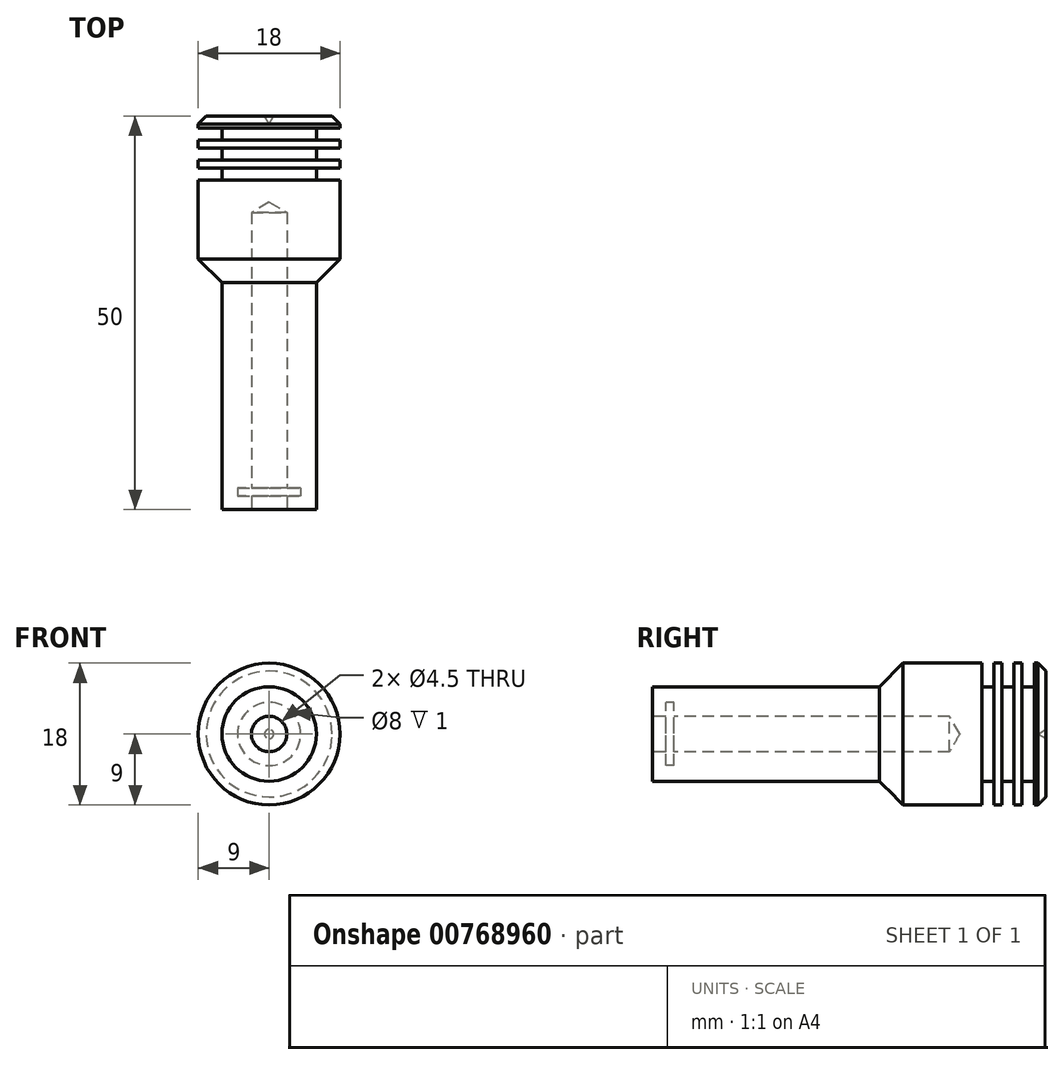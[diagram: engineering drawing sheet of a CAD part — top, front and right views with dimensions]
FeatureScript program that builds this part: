
annotation { "Feature Type Name" : "Feature", "Feature Type Description" : "" }
export const myFeature = defineFeature(function(context is Context, id is Id, definition is map)
    precondition{}
    {
        {
            var Q0;
            Q0=qCreatedBy(makeId("Right.planeOp"),FACE);
            var sketch = newSketch(context, id + "F0", { "sketchPlane" : qUnion([Q0])});
            skLineSegment(sketch, "E0", {"start": v(0, 6) * mm, "end": v(28.85, 6) * mm});
            skLineSegment(sketch, "E1", {"start": v(28.85, 6) * mm, "end": v(31.85, 9) * mm});
            skLineSegment(sketch, "E2", {"start": v(31.85, 9) * mm, "end": v(41.85, 9) * mm});
            skLineSegment(sketch, "E3", {"start": v(41.85, 9) * mm, "end": v(41.85, 6) * mm});
            skLineSegment(sketch, "E4", {"start": v(41.85, 6) * mm, "end": v(43.4, 6) * mm});
            skLineSegment(sketch, "E5", {"start": v(43.4, 6) * mm, "end": v(43.4, 9) * mm});
            skLineSegment(sketch, "E6", {"start": v(43.4, 9) * mm, "end": v(44.4, 9) * mm});
            skLineSegment(sketch, "E7", {"start": v(44.4, 9) * mm, "end": v(44.4, 6) * mm});
            skLineSegment(sketch, "E8", {"start": v(44.4, 6) * mm, "end": v(45.95, 6) * mm});
            skLineSegment(sketch, "E9", {"start": v(45.95, 6) * mm, "end": v(45.95, 9) * mm});
            skLineSegment(sketch, "E10", {"start": v(45.95, 9) * mm, "end": v(46.95, 9) * mm});
            skLineSegment(sketch, "E11", {"start": v(46.95, 9) * mm, "end": v(46.95, 6) * mm});
            skLineSegment(sketch, "E12", {"start": v(46.95, 6) * mm, "end": v(48.5, 6) * mm});
            skLineSegment(sketch, "E13", {"start": v(48.5, 6) * mm, "end": v(48.5, 9) * mm});
            skLineSegment(sketch, "E14", {"start": v(48.5, 9) * mm, "end": v(49, 9) * mm});
            skLineSegment(sketch, "E15", {"start": v(49, 9) * mm, "end": v(50, 8) * mm});
            skLineSegment(sketch, "E16", {"start": v(50, 8) * mm, "end": v(50, 0.58) * mm});
            skLineSegment(sketch, "E17", {"start": v(50, 0.58) * mm, "end": v(49, 0) * mm});
            skLineSegment(sketch, "E18", {"start": v(49, 0) * mm, "end": v(39.05, 0) * mm});
            skLineSegment(sketch, "E19", {"start": v(39.05, 0) * mm, "end": v(37.75, 2.25) * mm});
            skLineSegment(sketch, "E20", {"start": v(37.75, 2.25) * mm, "end": v(2.75, 2.25) * mm});
            skLineSegment(sketch, "E21", {"start": v(2.75, 2.25) * mm, "end": v(2.75, 4) * mm});
            skLineSegment(sketch, "E22", {"start": v(2.75, 4) * mm, "end": v(1.75, 4) * mm});
            skLineSegment(sketch, "E23", {"start": v(1.75, 4) * mm, "end": v(1.75, 2.25) * mm});
            skLineSegment(sketch, "E24", {"start": v(1.75, 2.25) * mm, "end": v(0, 2.25) * mm});
            skLineSegment(sketch, "E25", {"start": v(0, 6) * mm, "end": v(0, 2.25) * mm});
            skLineSegment(sketch, "E26", {"start": v(0, 0) * mm, "end": v(51.88, 0) * mm, "construction": true});
            skSolve(sketch);
        }
        {
            var Q0;
            Q0=makeQuery(id+"F0.imprint","IMPRINT",FACE,{"disambiguationData":[TD([[makeQuery(id+"F0.imprint","IMPRINT",EDGE,{"derivedFrom":sQuery(id+"F0.wireOp",EDGE,"E0")}),-1.0]])]});
            var Q1;
            Q1=sQuery(id+"F0.wireOp",EDGE,"E26");
            revolve(context, id + "F1", {"surfaceOperationType" : NewSurfaceOperationType.NEW, "entities" : qUnion([Q0]), "axis" : qUnion([Q1]), "revolveType" : RevolveType.FULL});
        }
    });
